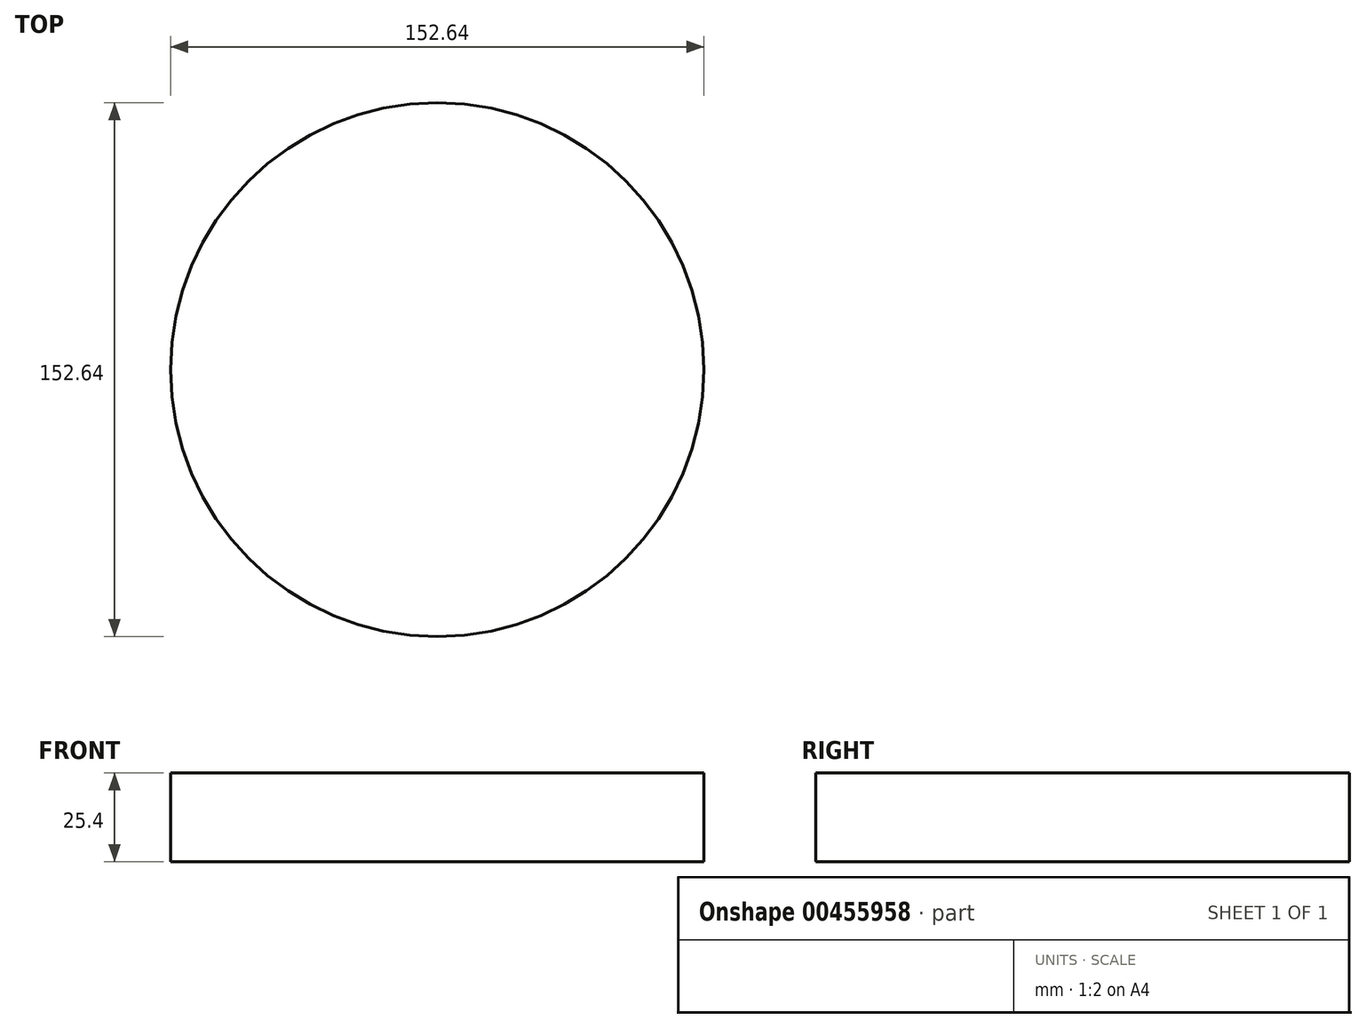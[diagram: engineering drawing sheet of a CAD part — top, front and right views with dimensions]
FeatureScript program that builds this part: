
annotation { "Feature Type Name" : "Feature", "Feature Type Description" : "" }
export const myFeature = defineFeature(function(context is Context, id is Id, definition is map)
    precondition{}
    {
        {
            var Q0;
            Q0=qCreatedBy(makeId("Top.planeOp"),FACE);
            var sketch = newSketch(context, id + "F0", { "sketchPlane" : qUnion([Q0])});
            skCircle(sketch, "E0", {"center": v(0, 0) * mm, "radius": 76.32 * mm});
            skSolve(sketch);
        }
        {
            var Q0;
            Q0=makeQuery(id+"F0.imprint","IMPRINT",FACE,{"disambiguationData":[TD([[makeQuery(id+"F0.imprint","IMPRINT",EDGE,{"derivedFrom":sQuery(id+"F0.wireOp",EDGE,"E0")}),1.0]])]});
            extrude(context, id + "F1", {"entities" : qUnion([Q0]), "depth" : 25.4 * mm});
        }
    });
